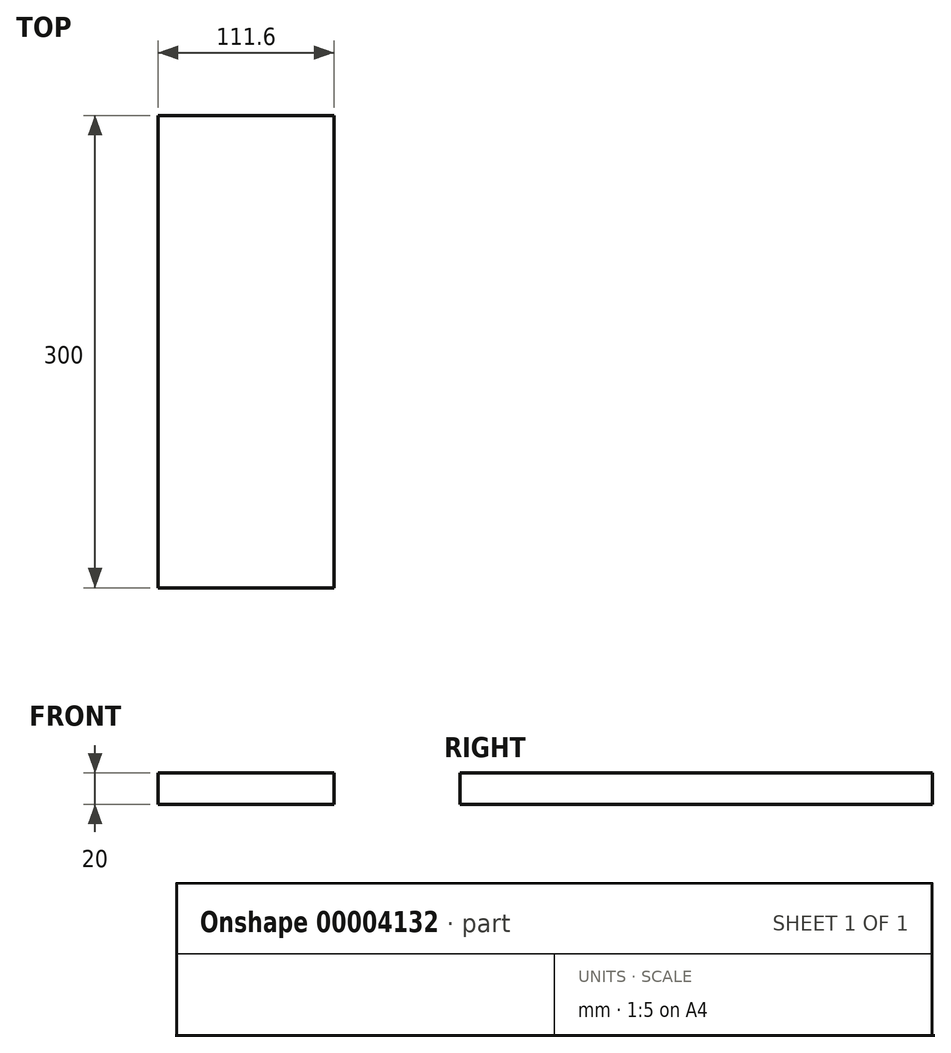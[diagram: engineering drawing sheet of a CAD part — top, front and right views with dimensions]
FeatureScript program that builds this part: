
annotation { "Feature Type Name" : "Feature", "Feature Type Description" : "" }
export const myFeature = defineFeature(function(context is Context, id is Id, definition is map)
    precondition{}
    {
        {
            var Q0;
            Q0=qCreatedBy(makeId("Top.planeOp"),FACE);
            var sketch = newSketch(context, id + "F0", { "sketchPlane" : qUnion([Q0])});
            skLineSegment(sketch, "E0.rect.bottom", {"start": v(55.8, -150) * mm, "end": v(-55.8, -150) * mm});
            skLineSegment(sketch, "E0.rect.top", {"start": v(55.8, 150) * mm, "end": v(-55.8, 150) * mm});
            skLineSegment(sketch, "E0.rect.left", {"start": v(55.8, -150) * mm, "end": v(55.8, 150) * mm});
            skLineSegment(sketch, "E0.rect.right", {"start": v(-55.8, -150) * mm, "end": v(-55.8, 150) * mm});
            skPoint(sketch, "E0.rect.middle", {"position": v(0, 0) * mm});
            skSolve(sketch);
        }
        {
            var Q0;
            Q0=makeQuery(id+"F0.imprint","IMPRINT",FACE,{"disambiguationData":[TD([[makeQuery(id+"F0.imprint","IMPRINT",EDGE,{"derivedFrom":sQuery(id+"F0.wireOp",EDGE,"E0.rect.bottom")}),-1.0]])]});
            extrude(context, id + "F1", {"entities" : qUnion([Q0]), "depth" : 20 * mm});
        }
    });
